# Revit family: PRD_AR_Sphns_Siphon_ZCMPX003
name_source: partatom
category: Plumbing Fixtures
revit_build: Autodesk Revit 2018 (Build: 20190510_1515(x64)
units: mm (PartAtom-declared; Revit-internal decimal feet)

## family parameters
Always vertical = No
Cut with Voids When Loaded = No
OmniClass Number = 23.45.00.00
OmniClass Title = Sanitary, Laundry, and Cleaning Equipment
Part Type = Normal
Room Calculation Point = No
Round Connector Dimension = Use Diameter
Shared = Yes
Work Plane-Based = Yes

## types (1)
- PRD_AR_Sphns_Siphon_ZCMPX003
    BIMObjectName = PRD_AR_Sphns_Siphon_ZCMPX003
    Default Elevation = 1219 mm
    Description = Siphon for squat pan, black colour, connection DN 100. Horizontal outlet.
    GrossWeight = 1.60 kg
    Manufacturer = KWC Group AG
    ManufacturerName = KWC Group AG
    ManufacturerURL = www.kwc.com
    Material = PRD_AR_SyntheticBlack
    Model = ZCMPX003
    ModelNumber = 2000102734
    ModelReference = ZCMPX003
    NBSDescription = Siphons
    NBSReference = Pr_60_45_78_78
    Name = Siphon ZCMPX003
    NetWeight = 1.50 kg
    URL = www.kwc.com
    WasteSize = 100 mm

## geometry (parser evidence)
native form markers: Sweep x2
no freeform markers — native parametric forms only
